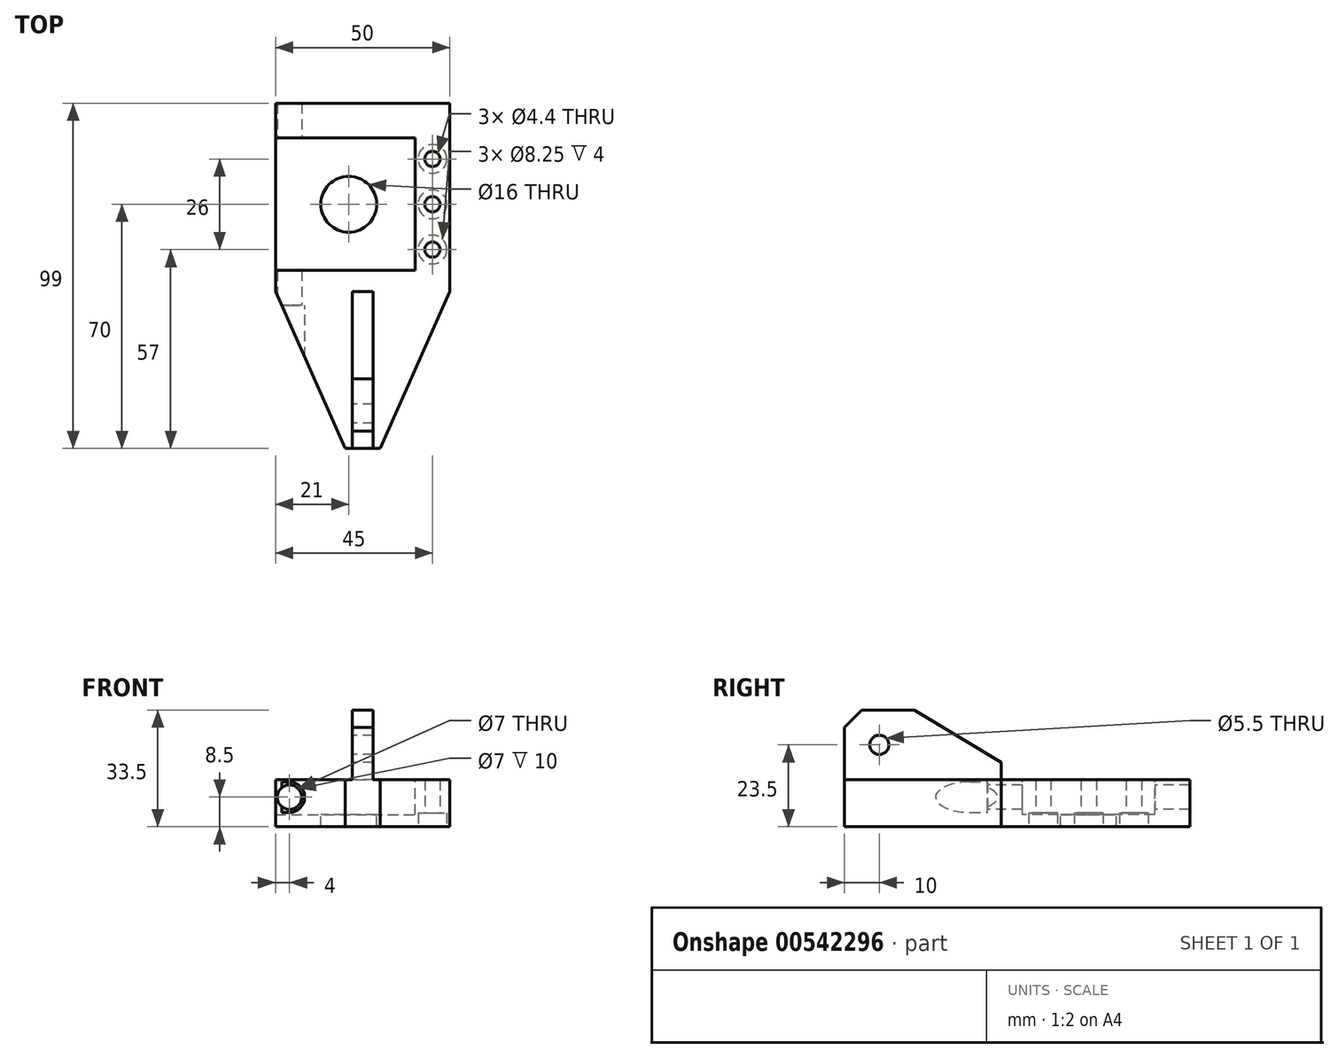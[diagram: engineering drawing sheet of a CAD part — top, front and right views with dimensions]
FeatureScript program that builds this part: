
annotation { "Feature Type Name" : "Feature", "Feature Type Description" : "" }
export const myFeature = defineFeature(function(context is Context, id is Id, definition is map)
    precondition{}
    {
        {
            var Q0;
            Q0=qCreatedBy(makeId("Top.planeOp"),FACE);
            var sketch = newSketch(context, id + "F0", { "sketchPlane" : qUnion([Q0])});
            skLineSegment(sketch, "E0", {"start": v(0, 50) * mm, "end": v(25, 50) * mm});
            skLineSegment(sketch, "E1", {"start": v(0, 50) * mm, "end": v(-25, 50) * mm});
            skLineSegment(sketch, "E2", {"start": v(-25, 50) * mm, "end": v(-25, 0) * mm});
            skLineSegment(sketch, "E3", {"start": v(25, 0) * mm, "end": v(25, 50) * mm});
            skLineSegment(sketch, "E4", {"start": v(5, -45) * mm, "end": v(-5, -45) * mm});
            skLineSegment(sketch, "E5", {"start": v(0, -45) * mm, "end": v(5, -45) * mm});
            skLineSegment(sketch, "E6", {"start": v(0, -45) * mm, "end": v(-5, -45) * mm});
            skLineSegment(sketch, "E7", {"start": v(-5, -45) * mm, "end": v(-25, 0) * mm});
            skLineSegment(sketch, "E8", {"start": v(5, -45) * mm, "end": v(25, 0) * mm});
            skSolve(sketch);
        }
        {
            var Q0;
            Q0=makeQuery(id+"F0.imprint","IMPRINT",FACE,{"disambiguationData":[TD([[makeQuery(id+"F0.imprint","IMPRINT",EDGE,{"derivedFrom":sQuery(id+"F0.wireOp",EDGE,"E0")}),-1.0]])]});
            extrude(context, id + "F1", {"entities" : qUnion([Q0]), "oppositeDirection" : true, "depth" : 13.5 * mm, "offsetDistance" : 25 * mm});
        }
        {
            var Q0;
            Q0=makeQuery(id+"F1.opExtrude","CAP_FACE",FACE,{"disambiguationData":[OSD([sQuery(id+"F0.wireOp",EDGE,"E0"),sQuery(id+"F0.wireOp",EDGE,"E1"),sQuery(id+"F0.wireOp",EDGE,"E2"),sQuery(id+"F0.wireOp",EDGE,"E3"),sQuery(id+"F0.wireOp",EDGE,"E5"),sQuery(id+"F0.wireOp",EDGE,"E6"),sQuery(id+"F0.wireOp",EDGE,"E7"),sQuery(id+"F0.wireOp",EDGE,"E8")])],"isStart":true});
            var sketch = newSketch(context, id + "F2", { "sketchPlane" : qUnion([Q0])});
            skLineSegment(sketch, "E9", {"start": v(-25, 44) * mm, "end": v(-25, 6) * mm});
            skLineSegment(sketch, "E10", {"start": v(-25, 6) * mm, "end": v(15, 6) * mm});
            skLineSegment(sketch, "E11", {"start": v(15, 6) * mm, "end": v(15, 44) * mm});
            skLineSegment(sketch, "E12", {"start": v(15, 44) * mm, "end": v(-25, 44) * mm});
            skSolve(sketch);
        }
        {
            var Q0;
            Q0=makeQuery(id+"F2.imprint","IMPRINT",FACE,{"disambiguationData":[TD([[makeQuery(id+"F2.imprint","IMPRINT",EDGE,{"derivedFrom":sQuery(id+"F2.wireOp",EDGE,"E9")}),1.0]])]});
            extrude(context, id + "F3", {"entities" : qUnion([Q0]), "operationType" : NewBodyOperationType.REMOVE, "oppositeDirection" : true, "depth" : 10 * mm, "offsetDistance" : 25 * mm});
        }
        {
            var Q0;
            Q0=qCreatedBy(makeId("Right.planeOp"),FACE);
            var sketch = newSketch(context, id + "F4", { "sketchPlane" : qUnion([Q0])});
            skLineSegment(sketch, "E13", {"start": v(0, 0) * mm, "end": v(-45, 0) * mm});
            skLineSegment(sketch, "E14", {"start": v(-45, 0) * mm, "end": v(-45, 20) * mm});
            skLineSegment(sketch, "E15", {"start": v(-45, 20) * mm, "end": v(-25, 20) * mm});
            skLineSegment(sketch, "E16", {"start": v(0, 0) * mm, "end": v(0, 5) * mm});
            skLineSegment(sketch, "E17", {"start": v(0, 5) * mm, "end": v(-25, 20) * mm});
            skCircle(sketch, "E18", {"center": v(-35, 10) * mm, "radius": 2.75 * mm});
            skSolve(sketch);
        }
        {
            var Q0;
            Q0=makeQuery(id+"F4.imprint","IMPRINT",FACE,{"disambiguationData":[TD([[makeQuery(id+"F4.imprint","IMPRINT",EDGE,{"derivedFrom":sQuery(id+"F4.wireOp",EDGE,"E13")}),-1.0]])]});
            extrude(context, id + "F5", {"entities" : qUnion([Q0]), "operationType" : NewBodyOperationType.ADD, "endBound" : BoundingType.SYMMETRIC, "depth" : 6 * mm, "offsetDistance" : 25 * mm});
        }
        {
            var Q0;
            Q0=makeQuery(id+"F5.opExtrude","SWEPT_EDGE",EDGE,{"disambiguationData":[OSD([sQuery(id+"F4.wireOp",EDGE,"E14"),sQuery(id+"F4.wireOp",EDGE,"E15")])]});
            chamfer(context, id + "F6", {"entities" : qUnion([Q0]), "width" : 5 * mm, "tangentPropagation" : true});
        }
        {
            var Q0;
            Q0=makeQuery(id+"F1.opExtrude","CAP_FACE",FACE,{"disambiguationData":[OSD([sQuery(id+"F0.wireOp",EDGE,"E0"),sQuery(id+"F0.wireOp",EDGE,"E1"),sQuery(id+"F0.wireOp",EDGE,"E2"),sQuery(id+"F0.wireOp",EDGE,"E3"),sQuery(id+"F0.wireOp",EDGE,"E5"),sQuery(id+"F0.wireOp",EDGE,"E6"),sQuery(id+"F0.wireOp",EDGE,"E7"),sQuery(id+"F0.wireOp",EDGE,"E8")])],"isStart":false});
            var sketch = newSketch(context, id + "F7", { "sketchPlane" : qUnion([Q0])});
            skLineSegment(sketch, "E19", {"start": v(25, -50) * mm, "end": v(20, -50) * mm});
            skLineSegment(sketch, "E20", {"start": v(20, -50) * mm, "end": v(20, -44) * mm});
            skLineSegment(sketch, "E21", {"start": v(20, -25) * mm, "end": v(5.6, -25) * mm});
            skPoint(sketch, "E21.endSnap0", {"position": v(20, -25) * mm});
            skLineSegment(sketch, "E22", {"start": v(20, -25) * mm, "end": v(20, -12) * mm});
            skLineSegment(sketch, "E23", {"start": v(20, -44) * mm, "end": v(5.6, -44) * mm});
            skLineSegment(sketch, "E24", {"start": v(5.6, -44) * mm, "end": v(5.6, -25) * mm});
            skLineSegment(sketch, "E25", {"start": v(20, -25) * mm, "end": v(20, -38) * mm});
            skSolve(sketch);
        }
        {
            var Q0;
            Q0=sQuery(id+"F7.wireOp",VERTEX,"1HJmEYKH-yNSV-Nryp-jSeX-Sqj1fZBOQwgL.start");
            var Q1;
            Q1=sQuery(id+"F7.wireOp",VERTEX,"E21.endSnap0");
            var Q2;
            Q2=sQuery(id+"F7.wireOp",VERTEX,"qZBesLjW-9xlX-z0kq-wGyA-M2MoXzIFqIkk.start");
            var Q3;
            Q3=sQuery(id+"F7.wireOp",VERTEX,"E22.end");
            var Q4;
            Q4=sQuery(id+"F7.wireOp",VERTEX,"E25.end");
            var Q5;
            Q5=makeQuery(id+"F1.opExtrude","SWEPT_BODY",BODY,{"disambiguationData":[OSD([sQuery(id+"F0.wireOp",EDGE,"E0"),sQuery(id+"F0.wireOp",EDGE,"E1"),sQuery(id+"F0.wireOp",EDGE,"E2"),sQuery(id+"F0.wireOp",EDGE,"E3"),sQuery(id+"F0.wireOp",EDGE,"E5"),sQuery(id+"F0.wireOp",EDGE,"E6"),sQuery(id+"F0.wireOp",EDGE,"E7"),sQuery(id+"F0.wireOp",EDGE,"E8")])]});
            hole(context, id + "F8", {"style" : HoleStyle.C_BORE, "endStyle" : HoleEndStyle.THROUGH, "standardTappedOrClearance" : lookupTablePath({ "standard" : "ISO", "fit" : "Normal", "size" : "M4", "type" : "Clearance" }), "standardBlindInLast" : lookupTablePath({ "fit" : "Standard", "standard" : "ISO", "size" : "M4", "type" : "Clearance" }), "holeDiameter" : 4.4 * mm, "cBoreDiameter" : 8.25 * mm, "cBoreDepth" : 4 * mm, "isTappedThrough" : true, "tappedDepth" : 9.9 * mm, "tapClearance" : 3, "startFromSketch" : true, "locations" : qUnion([Q0, Q1, Q2, Q3, Q4]), "scope" : qUnion([Q5])});
        }
        {
            var Q0;
            Q0=makeQuery(id+"F3.boolean.opBoolean","COPY",FACE,{"derivedFrom":makeQuery(id+"F3.opExtrude","SWEPT_FACE",FACE,{"disambiguationData":[OSD([sQuery(id+"F2.wireOp",EDGE,"E10")])]})});
            cPlane(context, id + "F9", {"entities" : qUnion([Q0]), "cplaneType" : CPlaneType.OFFSET, "offset" : 10 * mm, "oppositeDirection" : true, "width" : 150 * mm, "height" : 150 * mm});
        }
        {
            var Q0;
            Q0=qCreatedBy(id+"F9.planeOp",FACE);
            var sketch = newSketch(context, id + "F10", { "sketchPlane" : qUnion([Q0])});
            skLineSegment(sketch, "E26", {"start": v(25, -0.6) * mm, "end": v(25, -9.4) * mm});
            skArc(sketch, "E27", {"start": v(21, -0.6) * mm, "mid": v(16.6, -5) * mm, "end": v(21, -9.4) * mm});
            skLineSegment(sketch, "E28", {"start": v(21, -0.6) * mm, "end": v(25, -0.6) * mm});
            skLineSegment(sketch, "E29", {"start": v(21, -9.4) * mm, "end": v(25, -9.4) * mm});
            skSolve(sketch);
        }
        {
            var Q0;
            Q0=makeQuery(id+"F10.imprint","IMPRINT",FACE,{"disambiguationData":[TD([[makeQuery(id+"F10.imprint","IMPRINT",EDGE,{"derivedFrom":sQuery(id+"F10.wireOp",EDGE,"E26")}),-1.0]])]});
            extrude(context, id + "F11", {"entities" : qUnion([Q0]), "operationType" : NewBodyOperationType.REMOVE, "endBound" : BoundingType.THROUGH_ALL, "oppositeDirection" : true, "depth" : 25 * mm, "offsetDistance" : 25 * mm});
        }
        {
            var Q0;
            Q0=qCreatedBy(id+"F9.planeOp",FACE);
            var sketch = newSketch(context, id + "F12", { "sketchPlane" : qUnion([Q0])});
            skLineSegment(sketch, "E30", {"start": v(0, 0) * mm, "end": v(25, 0) * mm});
            skLineSegment(sketch, "E31", {"start": v(25, 0) * mm, "end": v(25, -10) * mm});
            skLineSegment(sketch, "E32", {"start": v(25, -5) * mm, "end": v(21, -5) * mm});
            skSolve(sketch);
        }
        {
            var Q0;
            Q0=sQuery(id+"F12.wireOp",VERTEX,"E32.end");
            var Q1;
            Q1=makeQuery(id+"F1.opExtrude","SWEPT_BODY",BODY,{"disambiguationData":[OSD([sQuery(id+"F0.wireOp",EDGE,"E0"),sQuery(id+"F0.wireOp",EDGE,"E1"),sQuery(id+"F0.wireOp",EDGE,"E2"),sQuery(id+"F0.wireOp",EDGE,"E3"),sQuery(id+"F0.wireOp",EDGE,"E5"),sQuery(id+"F0.wireOp",EDGE,"E6"),sQuery(id+"F0.wireOp",EDGE,"E7"),sQuery(id+"F0.wireOp",EDGE,"E8")])]});
            hole(context, id + "F13", {"style" : HoleStyle.SIMPLE, "endStyle" : HoleEndStyle.THROUGH, "oppositeDirection" : true, "holeDiameter" : 7 * mm, "isTappedThrough" : true, "tappedDepth" : 9.9 * mm, "tapClearance" : 3, "startFromSketch" : true, "locations" : qUnion([Q0]), "scope" : qUnion([Q1])});
        }
        {
            var Q0;
            Q0=makeQuery(id+"F1.opExtrude","SWEPT_FACE",FACE,{"disambiguationData":[OSD([sQuery(id+"F0.wireOp",EDGE,"E0"),sQuery(id+"F0.wireOp",EDGE,"E1")])]});
            var sketch = newSketch(context, id + "F14", { "sketchPlane" : qUnion([Q0])});
            skLineSegment(sketch, "E33.bottom", {"start": v(-25, -13.5) * mm, "end": v(25, -13.5) * mm});
            skLineSegment(sketch, "E33.top", {"start": v(-25, 0) * mm, "end": v(25, 0) * mm});
            skLineSegment(sketch, "E33.left", {"start": v(-25, -13.5) * mm, "end": v(-25, 0) * mm});
            skLineSegment(sketch, "E33.right", {"start": v(25, -13.5) * mm, "end": v(25, 0) * mm});
            skSolve(sketch);
        }
        {
            var Q0;
            Q0=makeQuery(id+"F14.imprint","IMPRINT",FACE,{"disambiguationData":[TD([[makeQuery(id+"F14.imprint","IMPRINT",EDGE,{"derivedFrom":sQuery(id+"F14.wireOp",EDGE,"E33.bottom")}),-1.0]])]});
            extrude(context, id + "F15", {"entities" : qUnion([Q0]), "operationType" : NewBodyOperationType.ADD, "depth" : 4 * mm, "offsetDistance" : 25 * mm});
        }
        {
            var Q0;
            Q0=makeQuery(id+"F3.boolean.opBoolean","COPY",FACE,{"derivedFrom":makeQuery(id+"F3.opExtrude","CAP_FACE",FACE,{"disambiguationData":[OSD([sQuery(id+"F2.wireOp",EDGE,"E9"),sQuery(id+"F2.wireOp",EDGE,"E10"),sQuery(id+"F2.wireOp",EDGE,"E11"),sQuery(id+"F2.wireOp",EDGE,"E12")])],"isStart":false})});
            var sketch = newSketch(context, id + "F16", { "sketchPlane" : qUnion([Q0])});
            skPoint(sketch, "E34.endSnap0", {"position": v(15, 25) * mm});
            skCircle(sketch, "E35", {"center": v(-4, 25) * mm, "radius": 8 * mm});
            skSolve(sketch);
        }
        {
            var Q0;
            Q0=makeQuery(id+"F16.imprint","IMPRINT",FACE,{"disambiguationData":[TD([[makeQuery(id+"F16.imprint","IMPRINT",EDGE,{"derivedFrom":sQuery(id+"F16.wireOp",EDGE,"E35")}),1.0]])]});
            var Q1;
            Q1=makeQuery(id+"F15.boolean.opBoolean","MERGE",FACE,{"derivedFrom":[makeQuery(id+"F1.opExtrude","CAP_FACE",FACE,{"disambiguationData":[OSD([sQuery(id+"F0.wireOp",EDGE,"E0"),sQuery(id+"F0.wireOp",EDGE,"E1"),sQuery(id+"F0.wireOp",EDGE,"E2"),sQuery(id+"F0.wireOp",EDGE,"E3"),sQuery(id+"F0.wireOp",EDGE,"E5"),sQuery(id+"F0.wireOp",EDGE,"E6"),sQuery(id+"F0.wireOp",EDGE,"E7"),sQuery(id+"F0.wireOp",EDGE,"E8")])],"isStart":false}),makeQuery(id+"F15.opExtrude","SWEPT_FACE",FACE,{"disambiguationData":[OSD([sQuery(id+"F14.wireOp",EDGE,"E33.bottom")])]})]});
            extrude(context, id + "F17", {"entities" : qUnion([Q0]), "operationType" : NewBodyOperationType.REMOVE, "endBound" : BoundingType.UP_TO_SURFACE, "oppositeDirection" : true, "depth" : 25 * mm, "endBoundEntityFace" : qUnion([Q1]), "offsetDistance" : 25 * mm});
        }
    });
